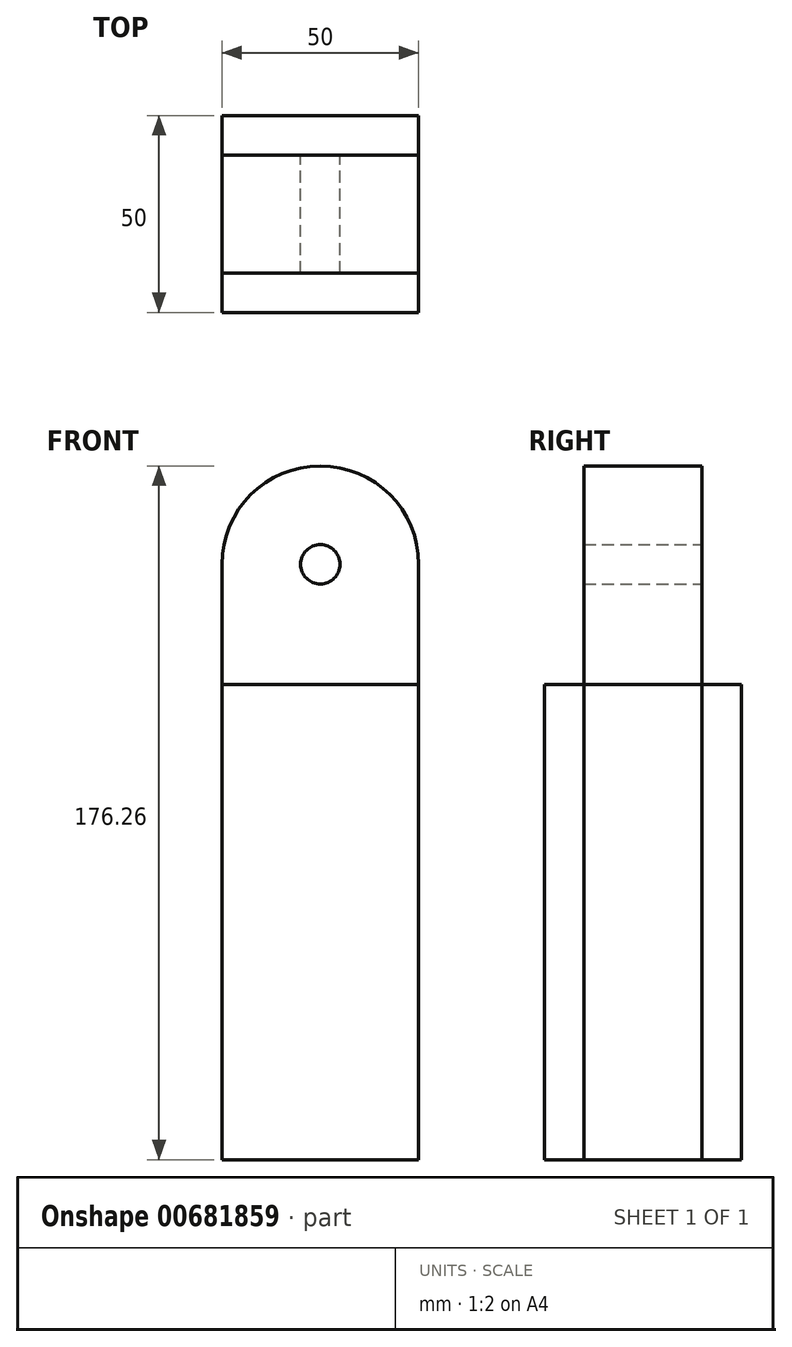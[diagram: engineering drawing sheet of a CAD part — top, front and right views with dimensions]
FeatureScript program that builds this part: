
annotation { "Feature Type Name" : "Feature", "Feature Type Description" : "" }
export const myFeature = defineFeature(function(context is Context, id is Id, definition is map)
    precondition{}
    {
        {
            var Q0;
            Q0=qCreatedBy(makeId("Front.planeOp"),FACE);
            var sketch = newSketch(context, id + "F0", { "sketchPlane" : qUnion([Q0])});
            skLineSegment(sketch, "E0.top", {"start": v(-82.83, -82.72) * mm, "end": v(-32.83, -82.72) * mm});
            skLineSegment(sketch, "E0.left", {"start": v(-82.83, 68.54) * mm, "end": v(-82.83, -82.72) * mm});
            skLineSegment(sketch, "E0.right", {"start": v(-32.83, 68.54) * mm, "end": v(-32.83, -82.72) * mm});
            skCircle(sketch, "E1", {"center": v(-57.83, 68.54) * mm, "radius": 5 * mm});
            skCircle(sketch, "E2", {"center": v(-57.83, 68.54) * mm, "radius": 25 * mm});
            skLineSegment(sketch, "E3", {"start": v(-82.83, 37.98) * mm, "end": v(-32.83, 37.98) * mm});
            skSolve(sketch);
        }
        {
            var Q0;
            Q0=makeQuery(id+"F0.imprint","IMPRINT",FACE,{"disambiguationData":[TD([[makeQuery(id+"F0.imprint","IMPRINT",EDGE,{"derivedFrom":sQuery(id+"F0.wireOp",EDGE,"E0.top")}),1.0]])]});
            extrude(context, id + "F1", {"entities" : qUnion([Q0]), "endBound" : BoundingType.SYMMETRIC, "depth" : 50 * mm, "offsetDistance" : 25 * mm});
        }
        {
            var Q0;
            Q0 = qSketchRegion(id + "F0", true);
            extrude(context, id + "F2", {"entities" : qUnion([Q0]), "endBound" : BoundingType.SYMMETRIC, "depth" : 30 * mm, "offsetDistance" : 25 * mm});
        }
    });
